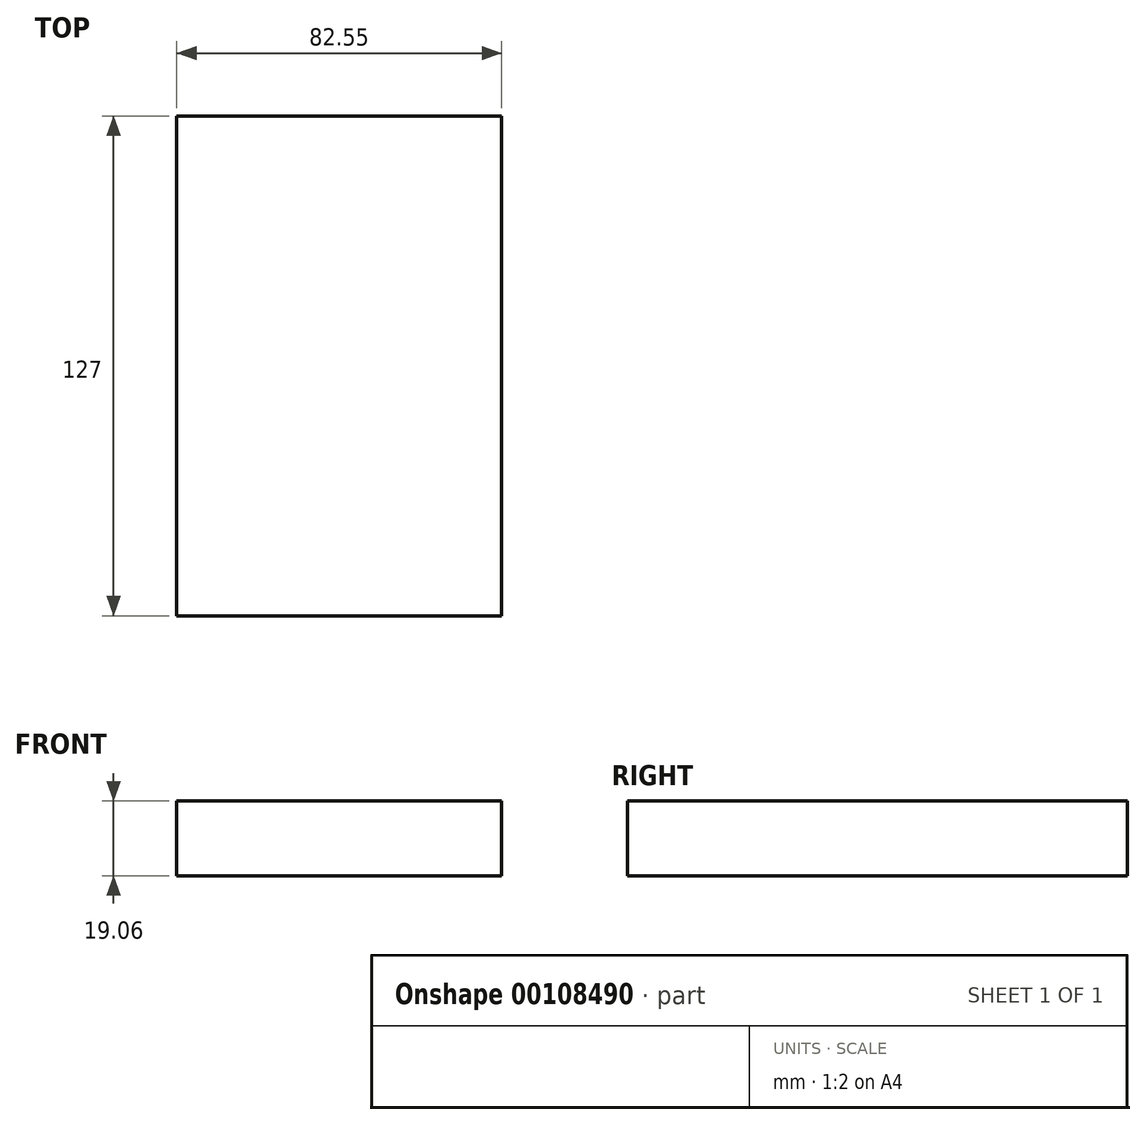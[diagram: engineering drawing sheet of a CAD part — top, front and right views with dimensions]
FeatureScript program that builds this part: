
annotation { "Feature Type Name" : "Feature", "Feature Type Description" : "" }
export const myFeature = defineFeature(function(context is Context, id is Id, definition is map)
    precondition{}
    {
        {
            var Q0;
            Q0=qCreatedBy(makeId("Front.planeOp"),FACE);
            var sketch = newSketch(context, id + "F0", { "sketchPlane" : qUnion([Q0])});
            skLineSegment(sketch, "E0.bottom", {"start": v(41.27, 9.53) * mm, "end": v(-41.28, 9.53) * mm});
            skLineSegment(sketch, "E0.top", {"start": v(41.28, -9.52) * mm, "end": v(-41.27, -9.52) * mm});
            skLineSegment(sketch, "E0.left", {"start": v(41.28, 9.53) * mm, "end": v(41.28, -9.52) * mm});
            skLineSegment(sketch, "E0.right", {"start": v(-41.28, 9.53) * mm, "end": v(-41.27, -9.52) * mm});
            skPoint(sketch, "E0.middle", {"position": v(0, 0) * mm});
            skLineSegment(sketch, "E1.bottom", {"start": v(111.13, 38.1) * mm, "end": v(60.32, 38.1) * mm});
            skLineSegment(sketch, "E1.top", {"start": v(111.13, 66.68) * mm, "end": v(60.32, 66.68) * mm});
            skLineSegment(sketch, "E1.left", {"start": v(111.13, 38.1) * mm, "end": v(111.13, 66.68) * mm});
            skLineSegment(sketch, "E1.right", {"start": v(60.32, 38.1) * mm, "end": v(60.32, 66.68) * mm});
            skPoint(sketch, "E1.middle", {"position": v(85.73, 52.39) * mm});
            skLineSegment(sketch, "E2", {"start": v(41.27, 9.53) * mm, "end": v(41.27, 27) * mm});
            skArc(sketch, "E3", {"start": v(41.27, 27) * mm, "mid": v(45.92, 38.23) * mm, "end": v(57.15, 42.88) * mm});
            skLineSegment(sketch, "E4", {"start": v(57.15, 42.88) * mm, "end": v(85.73, 42.88) * mm});
            skLineSegment(sketch, "E5.0", {"start": v(57.15, 61.93) * mm, "end": v(85.73, 61.93) * mm});
            skArc(sketch, "E5.1", {"start": v(22.23, 27) * mm, "mid": v(32.45, 51.7) * mm, "end": v(57.15, 61.93) * mm});
            skLineSegment(sketch, "E5.2", {"start": v(22.22, 9.53) * mm, "end": v(22.22, 27) * mm});
            skLineSegment(sketch, "E6", {"start": v(85.73, 42.88) * mm, "end": v(85.73, 61.93) * mm});
            skFitSpline(sketch, "E7", {"points": [v(-41.28, 9.52) * mm, v(57.15, 61.93) * mm], "startDerivative": vector(66.14, 105.5) * mm, "endDerivative": vector(108.54, -0.4) * mm});
            skSolve(sketch);
        }
        {
            var Q0;
            Q0=makeQuery(id+"F0.imprint","IMPRINT",FACE,{"disambiguationData":[TD([[makeQuery(id+"F0.imprint","IMPRINT",EDGE,{"derivedFrom":sQuery(id+"F0.wireOp",EDGE,"E0.top")}),-1.0]])]});
            extrude(context, id + "F1", {"entities" : qUnion([Q0]), "depth" : 127 * mm, "symmetric" : true});
        }
    });
